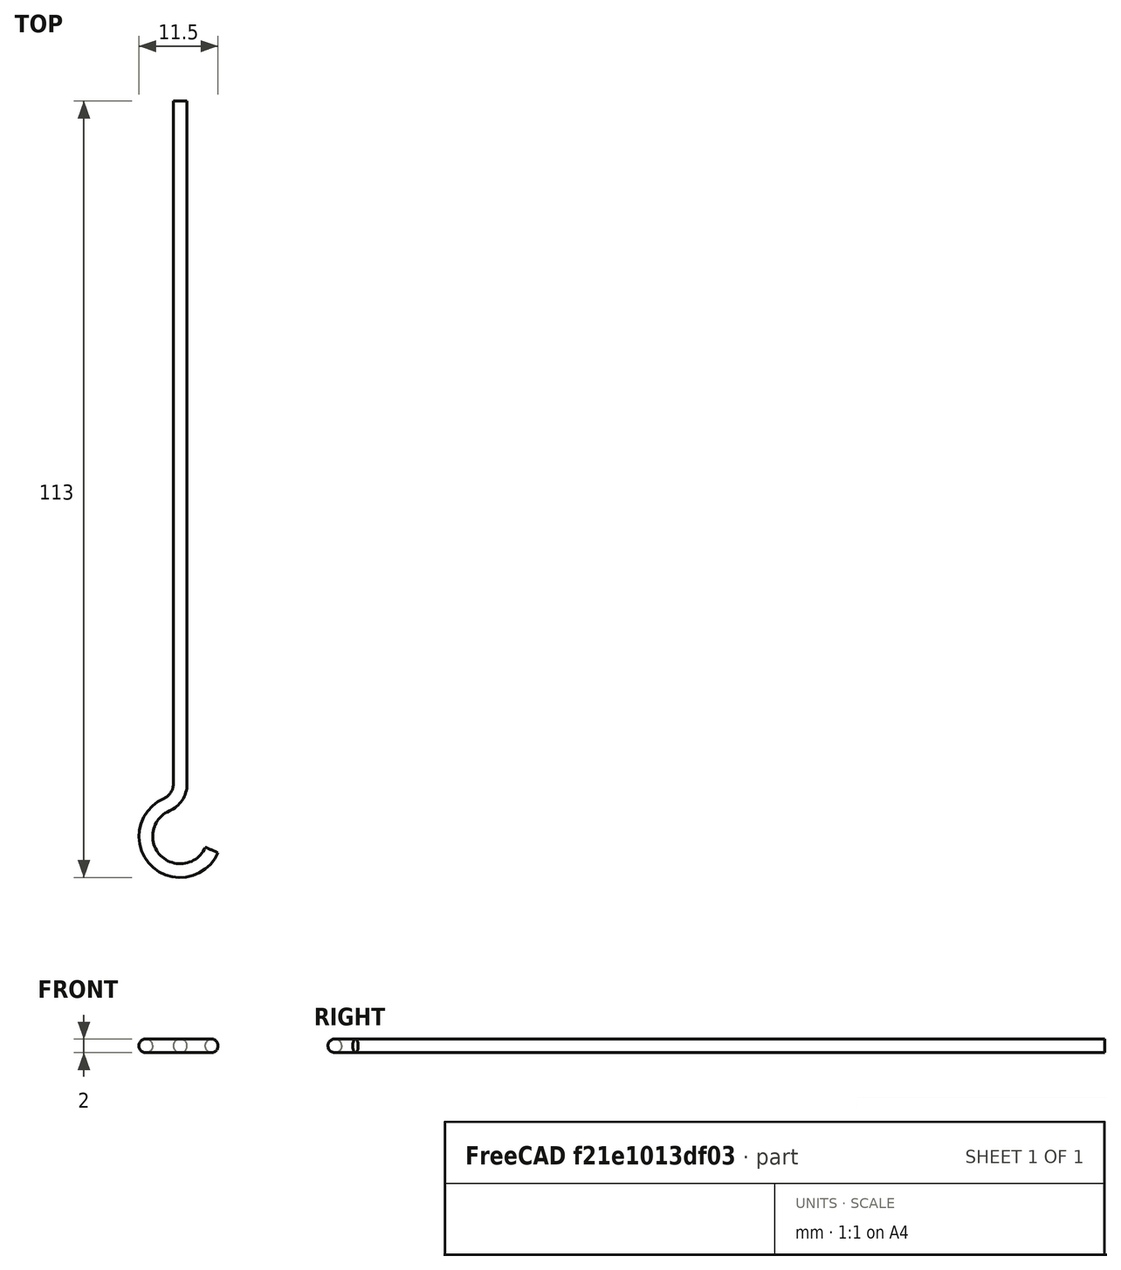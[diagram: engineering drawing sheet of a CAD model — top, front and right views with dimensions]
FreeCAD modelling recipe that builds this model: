
FCSTD DOCUMENT  (FreeCAD 0.18.4R)
Label: hook
License: All rights reserved
LicenseURL: http://en.wikipedia.org/wiki/All_rights_reserved
objects: Sketcher::SketchObject×2, PartDesign::AdditivePipe×1, PartDesign::Body×1
note: 5 computed .brp shape members not serialized (recipe doc carries the construction recipe); baked Part::Feature solids carry a one-line shape summary decoded from their .brp

FEATURE [Sketcher::SketchObject] Sketch
  MapMode = 5
  Support = -> [XY_Plane]
  sketch-geometry (3):
    g0: LineSegment StartX=0 StartY=7.59321 StartZ=0 EndX=0 EndY=107 EndZ=0
    g1: ArcOfCircle CenterX=0 CenterY=0 CenterZ=0 NormalX=0 NormalY=0 NormalZ=1 AngleXU=0 Radius=5 StartAngle=1.97696 EndAngle=5.87167
    g2: ArcOfCircle CenterX=-3.26569 CenterY=7.59321 CenterZ=0 NormalX=0 NormalY=0 NormalZ=1 AngleXU=0 Radius=3.26569 StartAngle=5.11855 EndAngle=6.28319
  constraints (9):
    c: Vertical(g0)
    c: Coincident(g1,g-1)
    c: Tangent(g1,g2) = 1.5708
    c: Tangent(g0,g2) = -1.5708
    c: Radius(g1) = 5
    c: PointOnObject(g0,g-2)
    c: DistanceY(g1,g0) = 107
    c: DistanceY(g1,g1) = 2
    c: DistanceY(g1,g0) = 3
FEATURE [Sketcher::SketchObject] Sketch001
  AttachmentOffset = pos=(0,0,-70) rot=(0,0,1;0rad)
  MapMode = 5
  Placement = pos=(0,70,1.55e-14) rot=(1,0,0;1.5708rad)
  Support = -> [XZ_Plane]
  sketch-geometry (1):
    g0: Circle CenterX=0 CenterY=0 CenterZ=0 NormalX=0 NormalY=0 NormalZ=1 AngleXU=0 Radius=1
  constraints (2):
    c: Coincident(g0,g-1)
    c: Radius(g0) = 1
FEATURE [PartDesign::AdditivePipe] AdditivePipe
  AuxilleryCurvelinear = true
  AuxillerySpineTangent = false
  Binormal = (0,0,0)
  Mode = 0
  Placement = pos=(0,0,0) rot=(1,0,0;1.5708rad)
  Profile = -> Sketch001
  Spine = -> Sketch
  SpineTangent = false
  Transformation = 0
  Transition = 0
FEATURE [PartDesign::Body] Body
  Group = -> [Sketch,Sketch001,AdditivePipe]
  Origin = -> Origin
  Tip = -> AdditivePipe
